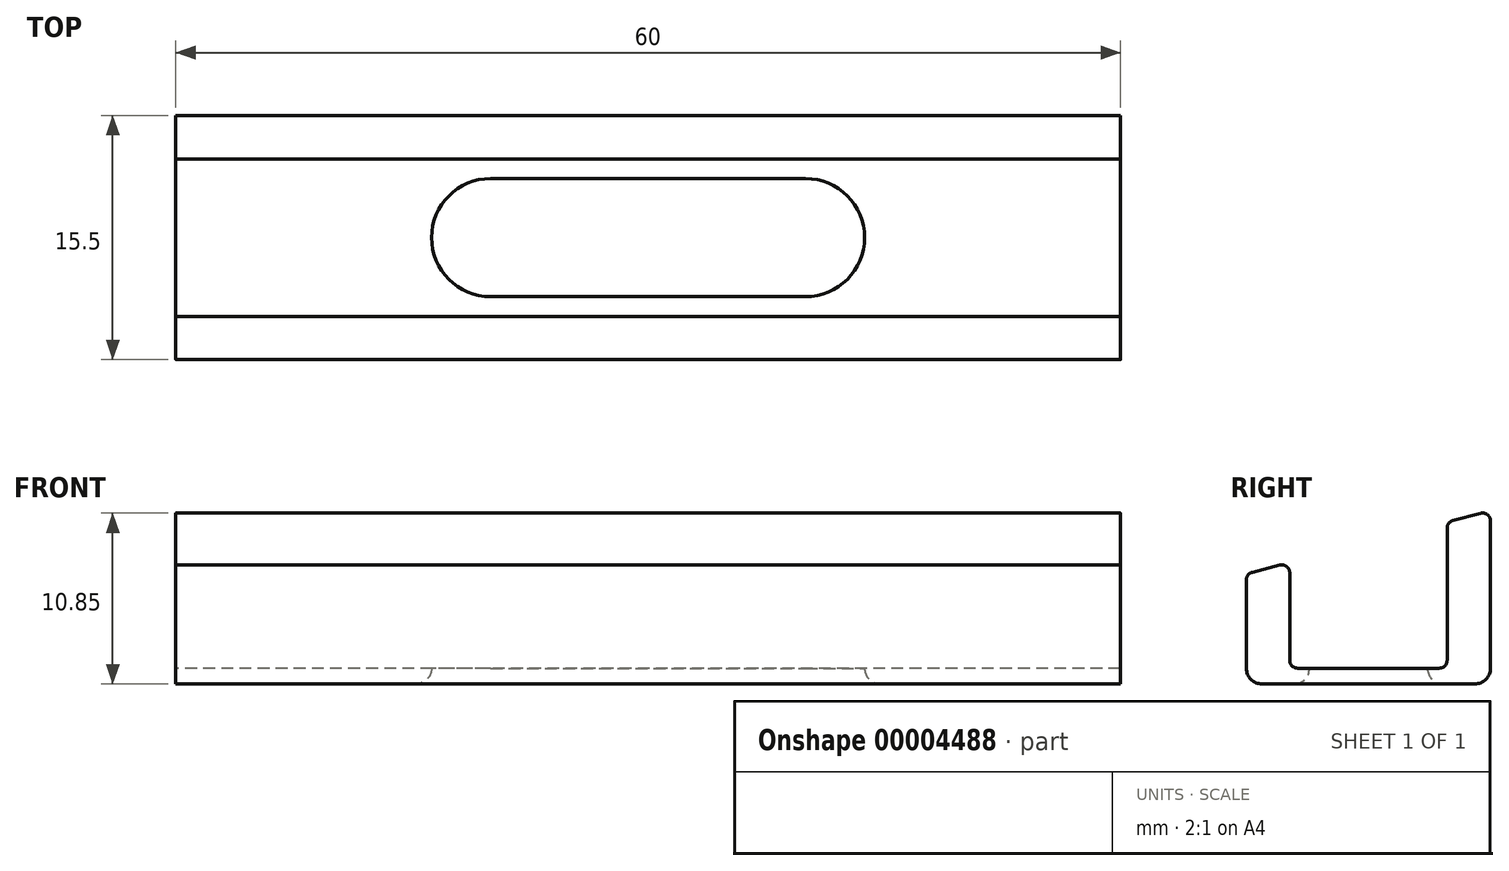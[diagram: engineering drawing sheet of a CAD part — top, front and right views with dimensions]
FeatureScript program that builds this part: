
annotation { "Feature Type Name" : "Feature", "Feature Type Description" : "" }
export const myFeature = defineFeature(function(context is Context, id is Id, definition is map)
    precondition{}
    {
        {
            var Q0;
            Q0=qCreatedBy(makeId("Right.planeOp"),FACE);
            var sketch = newSketch(context, id + "F0", { "sketchPlane" : qUnion([Q0])});
            skLineSegment(sketch, "E0", {"start": v(-1, 0) * mm, "end": v(-14.5, 0) * mm});
            skLineSegment(sketch, "E1", {"start": v(-15.5, 1) * mm, "end": v(-15.5, 6.61) * mm});
            skLineSegment(sketch, "E2", {"start": v(-15.12, 7.1) * mm, "end": v(-13.37, 7.55) * mm});
            skLineSegment(sketch, "E3", {"start": v(0, 10.35) * mm, "end": v(0, 1) * mm});
            skLineSegment(sketch, "E4", {"start": v(-12.75, 7.06) * mm, "end": v(-12.75, 1.5) * mm});
            skLineSegment(sketch, "E5", {"start": v(-12.25, 1) * mm, "end": v(-3.25, 1) * mm});
            skLineSegment(sketch, "E6", {"start": v(-2.75, 1.5) * mm, "end": v(-2.75, 9.9) * mm});
            skLineSegment(sketch, "E7.trimOffspring", {"start": v(-2.37, 10.39) * mm, "end": v(-0.62, 10.84) * mm});
            skPoint(sketch, "E8.visualSharp", {"position": v(-12.75, 1) * mm});
            skArc(sketch, "E8.filletArc", {"start": v(-12.75, 1.5) * mm, "mid": v(-12.6, 1.15) * mm, "end": v(-12.25, 1) * mm});
            skPoint(sketch, "E9.visualSharp", {"position": v(-2.75, 1) * mm});
            skArc(sketch, "E9.filletArc", {"start": v(-3.25, 1) * mm, "mid": v(-2.9, 1.15) * mm, "end": v(-2.75, 1.5) * mm});
            skPoint(sketch, "E10.visualSharp", {"position": v(-15.5, 0) * mm});
            skArc(sketch, "E10.filletArc", {"start": v(-15.5, 1) * mm, "mid": v(-15.2, 0.3) * mm, "end": v(-14.5, 0) * mm});
            skPoint(sketch, "E11.visualSharp", {"position": v(0, 0) * mm});
            skArc(sketch, "E11.filletArc", {"start": v(-1, 0) * mm, "mid": v(-0.3, 0.3) * mm, "end": v(0, 1) * mm});
            skPoint(sketch, "E12.visualSharp", {"position": v(-12.75, 7.7) * mm});
            skArc(sketch, "E12.filletArc", {"start": v(-12.75, 7.06) * mm, "mid": v(-12.94, 7.46) * mm, "end": v(-13.37, 7.55) * mm});
            skPoint(sketch, "E13.visualSharp", {"position": v(-15.5, 7) * mm});
            skArc(sketch, "E13.filletArc", {"start": v(-15.12, 7.1) * mm, "mid": v(-15.4, 6.92) * mm, "end": v(-15.5, 6.61) * mm});
            skPoint(sketch, "E14.visualSharp", {"position": v(-2.75, 10.3) * mm});
            skArc(sketch, "E14.filletArc", {"start": v(-2.37, 10.39) * mm, "mid": v(-2.65, 10.2) * mm, "end": v(-2.75, 9.9) * mm});
            skPoint(sketch, "E15.visualSharp", {"position": v(0, 11) * mm});
            skArc(sketch, "E15.filletArc", {"start": v(0, 10.35) * mm, "mid": v(-0.2, 10.75) * mm, "end": v(-0.62, 10.84) * mm});
            skSolve(sketch);
        }
        {
            var Q0;
            Q0=makeQuery(id+"F0.imprint","IMPRINT",FACE,{"disambiguationData":[TD([[makeQuery(id+"F0.imprint","IMPRINT",EDGE,{"derivedFrom":sQuery(id+"F0.wireOp",EDGE,"E0")}),-1.0]])]});
            extrude(context, id + "F1", {"entities" : qUnion([Q0]), "depth" : 60 * mm});
        }
        {
            var Q0;
            Q0=makeQuery(id+"F1.opExtrude","SWEPT_FACE",FACE,{"disambiguationData":[OSD([sQuery(id+"F0.wireOp",EDGE,"E5")])]});
            var sketch = newSketch(context, id + "F2", { "sketchPlane" : qUnion([Q0])});
            skLineSegment(sketch, "E16", {"start": v(20, -4) * mm, "end": v(40, -4) * mm});
            skLineSegment(sketch, "E17", {"start": v(20, -11.5) * mm, "end": v(40, -11.5) * mm});
            skArc(sketch, "E18", {"start": v(20, -4) * mm, "mid": v(16.25, -7.75) * mm, "end": v(20, -11.5) * mm});
            skArc(sketch, "E19", {"start": v(40, -4) * mm, "mid": v(43.75, -7.75) * mm, "end": v(40, -11.5) * mm});
            skLineSegment(sketch, "E20", {"start": v(30, -3.25) * mm, "end": v(30, -12.25) * mm, "construction": true});
            skLineSegment(sketch, "E21", {"start": v(20, -7.75) * mm, "end": v(40, -7.75) * mm, "construction": true});
            skLineSegment(sketch, "E22", {"start": v(0, -7.75) * mm, "end": v(60, -7.75) * mm, "construction": true});
            skLineSegment(sketch, "E23", {"start": v(20, -4) * mm, "end": v(20, -11.5) * mm, "construction": true});
            skLineSegment(sketch, "E24", {"start": v(16.25, -7.75) * mm, "end": v(43.75, -7.75) * mm, "construction": true});
            skSolve(sketch);
        }
        {
            var Q0;
            Q0=makeQuery(id+"F2.imprint","IMPRINT",FACE,{"disambiguationData":[TD([[makeQuery(id+"F2.imprint","IMPRINT",EDGE,{"derivedFrom":sQuery(id+"F2.wireOp",EDGE,"E16")}),-1.0]])]});
            extrude(context, id + "F3", {"entities" : qUnion([Q0]), "operationType" : NewBodyOperationType.REMOVE, "endBound" : BoundingType.THROUGH_ALL, "oppositeDirection" : true, "depth" : 25 * mm});
        }
        {
            var Q0;
            Q0=makeQuery(id+"F3.boolean.opBoolean","INTERSECT",EDGE,{"derivedFrom":[makeQuery(id+"F1.opExtrude","SWEPT_FACE",FACE,{"disambiguationData":[OSD([sQuery(id+"F0.wireOp",EDGE,"E0")])]}),makeQuery(id+"F3.opExtrude","SWEPT_FACE",FACE,{"disambiguationData":[OSD([sQuery(id+"F2.wireOp",EDGE,"E17")])]})]});
            fillet(context, id + "F4", {"entities" : qUnion([Q0]), "radius" : 1 * mm, "tangentPropagation" : true, "allowEdgeOverflow" : false});
        }
    });
